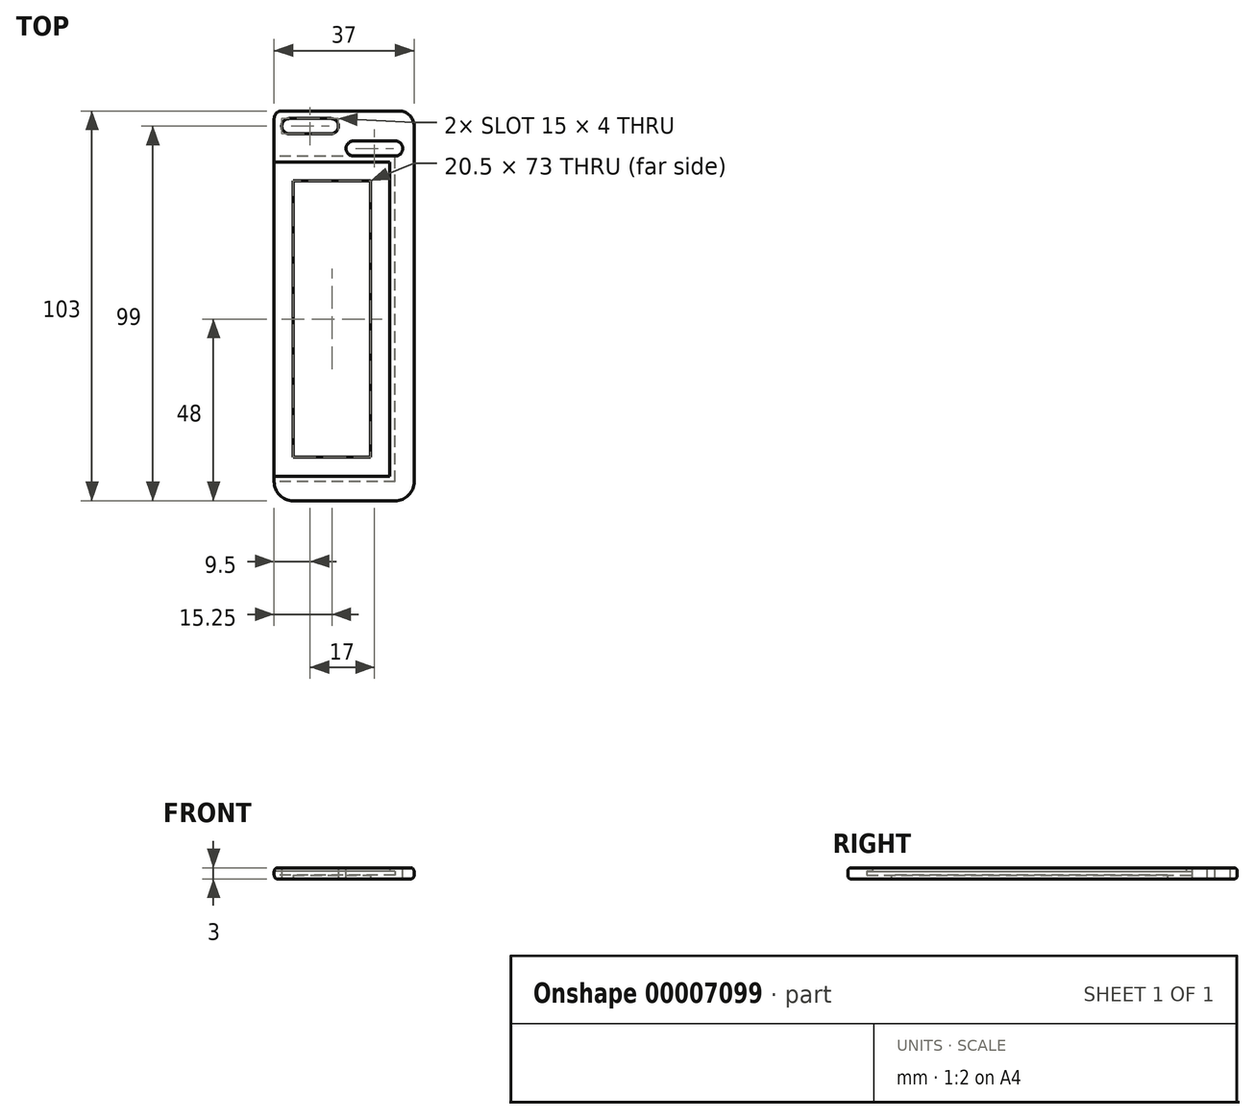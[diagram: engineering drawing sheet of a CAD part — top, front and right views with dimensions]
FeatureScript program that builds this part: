
annotation { "Feature Type Name" : "Feature", "Feature Type Description" : "" }
export const myFeature = defineFeature(function(context is Context, id is Id, definition is map)
    precondition{}
    {
        {
            var Q0;
            Q0=qCreatedBy(makeId("Top.planeOp"),FACE);
            var sketch = newSketch(context, id + "F0", { "sketchPlane" : qUnion([Q0])});
            skLineSegment(sketch, "E0.bottom", {"start": v(0, 0) * mm, "end": v(54, 0) * mm, "construction": true});
            skLineSegment(sketch, "E0.top", {"start": v(0, 86) * mm, "end": v(54, 86) * mm, "construction": true});
            skLineSegment(sketch, "E0.left", {"start": v(0, 0) * mm, "end": v(0, 86) * mm, "construction": true});
            skLineSegment(sketch, "E0.right", {"start": v(54, 0) * mm, "end": v(54, 86) * mm});
            skLineSegment(sketch, "E1", {"start": v(54, 0) * mm, "end": v(22, 0) * mm});
            skLineSegment(sketch, "E2", {"start": v(0, 43) * mm, "end": v(90.24, 43) * mm, "construction": true});
            skLineSegment(sketch, "E3.0.MirrorCS", {"start": v(54, 86) * mm, "end": v(22, 86) * mm});
            skLineSegment(sketch, "E4.0", {"start": v(59, 91) * mm, "end": v(22, 91) * mm});
            skLineSegment(sketch, "E4.1", {"start": v(59, -5) * mm, "end": v(59, 91) * mm});
            skLineSegment(sketch, "E4.2", {"start": v(59, -5) * mm, "end": v(22, -5) * mm});
            skLineSegment(sketch, "E5", {"start": v(22, 91) * mm, "end": v(22, 86) * mm});
            skLineSegment(sketch, "E6", {"start": v(22, -5) * mm, "end": v(22, 0) * mm});
            skSolve(sketch);
        }
        {
            var Q0;
            Q0 = qSketchRegion(id + "F0", true);
            extrude(context, id + "F1", {"entities" : qUnion([Q0]), "depth" : 1 * mm});
        }
        {
            var Q0;
            Q0=makeQuery(id+"F1.opExtrude","CAP_FACE",FACE,{"disambiguationData":[OSD([sQuery(id+"F0.wireOp",EDGE,"E0.right"),sQuery(id+"F0.wireOp",EDGE,"E1"),sQuery(id+"F0.wireOp",EDGE,"E3.0.MirrorCS"),sQuery(id+"F0.wireOp",EDGE,"E4.0"),sQuery(id+"F0.wireOp",EDGE,"E4.1"),sQuery(id+"F0.wireOp",EDGE,"E4.2"),sQuery(id+"F0.wireOp",EDGE,"E5"),sQuery(id+"F0.wireOp",EDGE,"E6")])],"isStart":false});
            var sketch = newSketch(context, id + "F2", { "sketchPlane" : qUnion([Q0])});
            skLineSegment(sketch, "E7.0", {"start": v(54, 86) * mm, "end": v(22, 86) * mm, "construction": true});
            skLineSegment(sketch, "E7.1", {"start": v(54, 0) * mm, "end": v(54, 86) * mm, "construction": true});
            skLineSegment(sketch, "E7.2", {"start": v(54, 0) * mm, "end": v(22, 0) * mm, "construction": true});
            skLineSegment(sketch, "E8.0", {"start": v(52.5, 84.5) * mm, "end": v(22, 84.5) * mm});
            skLineSegment(sketch, "E8.1", {"start": v(52.5, 1.5) * mm, "end": v(52.5, 84.5) * mm});
            skLineSegment(sketch, "E8.2", {"start": v(52.5, 1.5) * mm, "end": v(22, 1.5) * mm});
            skLineSegment(sketch, "E9.0", {"start": v(59, 91) * mm, "end": v(22, 91) * mm});
            skLineSegment(sketch, "E9.1", {"start": v(59, -5) * mm, "end": v(59, 91) * mm});
            skLineSegment(sketch, "E9.2", {"start": v(59, -5) * mm, "end": v(22, -5) * mm});
            skLineSegment(sketch, "E10", {"start": v(22, 84.5) * mm, "end": v(22, 91) * mm});
            skLineSegment(sketch, "E11", {"start": v(22, 1.5) * mm, "end": v(22, -5) * mm});
            skSolve(sketch);
        }
        {
            var Q0;
            Q0 = qSketchRegion(id + "F2", true);
            extrude(context, id + "F3", {"entities" : qUnion([Q0]), "operationType" : NewBodyOperationType.ADD, "depth" : 1 * mm});
        }
        {
            var Q0;
            Q0=makeQuery(id+"F1.opExtrude","CAP_FACE",FACE,{"disambiguationData":[OSD([sQuery(id+"F0.wireOp",EDGE,"E0.right"),sQuery(id+"F0.wireOp",EDGE,"E1"),sQuery(id+"F0.wireOp",EDGE,"E3.0.MirrorCS"),sQuery(id+"F0.wireOp",EDGE,"E4.0"),sQuery(id+"F0.wireOp",EDGE,"E4.1"),sQuery(id+"F0.wireOp",EDGE,"E4.2"),sQuery(id+"F0.wireOp",EDGE,"E5"),sQuery(id+"F0.wireOp",EDGE,"E6")])],"isStart":true});
            var sketch = newSketch(context, id + "F4", { "sketchPlane" : qUnion([Q0])});
            skLineSegment(sketch, "E12.0", {"start": v(59, 5) * mm, "end": v(59, -91) * mm});
            skLineSegment(sketch, "E12.1", {"start": v(59, 5) * mm, "end": v(22, 5) * mm});
            skLineSegment(sketch, "E12.2", {"start": v(59, -91) * mm, "end": v(22, -91) * mm});
            skLineSegment(sketch, "E12.3", {"start": v(22, -91) * mm, "end": v(22, -86) * mm});
            skLineSegment(sketch, "E12.4", {"start": v(22, -84.5) * mm, "end": v(22, -86) * mm});
            skLineSegment(sketch, "E12.5", {"start": v(52.5, -84.5) * mm, "end": v(22, -84.5) * mm});
            skLineSegment(sketch, "E12.6", {"start": v(52.5, -1.5) * mm, "end": v(52.5, -84.5) * mm});
            skLineSegment(sketch, "E12.7", {"start": v(52.5, -1.5) * mm, "end": v(22, -1.5) * mm});
            skLineSegment(sketch, "E12.8", {"start": v(22, 5) * mm, "end": v(22, 0) * mm});
            skLineSegment(sketch, "E12.9", {"start": v(22, -1.5) * mm, "end": v(22, 0) * mm});
            skSolve(sketch);
        }
        {
            var Q0;
            Q0 = qSketchRegion(id + "F4", true);
            extrude(context, id + "F5", {"entities" : qUnion([Q0]), "operationType" : NewBodyOperationType.ADD, "depth" : 1 * mm});
        }
        {
            var Q0;
            Q0=qCreatedBy(makeId("Top.planeOp"),FACE);
            var sketch = newSketch(context, id + "F6", { "sketchPlane" : qUnion([Q0])});
            skLineSegment(sketch, "E13.0", {"start": v(59, 91) * mm, "end": v(22, 91) * mm, "construction": true});
            skLineSegment(sketch, "E14.bottom", {"start": v(22, 91) * mm, "end": v(59, 91) * mm});
            skLineSegment(sketch, "E14.top", {"start": v(24, 98) * mm, "end": v(55, 98) * mm});
            skLineSegment(sketch, "E14.left", {"start": v(22, 91) * mm, "end": v(22, 96) * mm});
            skLineSegment(sketch, "E14.right", {"start": v(59, 91) * mm, "end": v(59, 94) * mm});
            skLineSegment(sketch, "E15", {"start": v(27, 75.52) * mm, "end": v(27, 108.91) * mm, "construction": true});
            skLineSegment(sketch, "E16.bottom", {"start": v(26, 96) * mm, "end": v(37, 96) * mm});
            skLineSegment(sketch, "E16.top", {"start": v(26, 92) * mm, "end": v(37, 92) * mm});
            skLineSegment(sketch, "E16.left", {"start": v(24, 94) * mm, "end": v(24, 94) * mm});
            skLineSegment(sketch, "E16.right", {"start": v(39, 94) * mm, "end": v(39, 94) * mm});
            skPoint(sketch, "E17.visualSharp", {"position": v(59, 98) * mm});
            skArc(sketch, "E17.filletArc", {"start": v(59, 94) * mm, "mid": v(57.83, 96.83) * mm, "end": v(55, 98) * mm});
            skPoint(sketch, "E18.visualSharp", {"position": v(22, 98) * mm});
            skArc(sketch, "E18.filletArc", {"start": v(24, 98) * mm, "mid": v(22.59, 97.41) * mm, "end": v(22, 96) * mm});
            skPoint(sketch, "E19.visualSharp", {"position": v(39, 96) * mm});
            skArc(sketch, "E19.filletArc", {"start": v(39, 94) * mm, "mid": v(38.41, 95.41) * mm, "end": v(37, 96) * mm});
            skPoint(sketch, "E20.visualSharp", {"position": v(39, 92) * mm});
            skArc(sketch, "E20.filletArc", {"start": v(37, 92) * mm, "mid": v(38.41, 92.59) * mm, "end": v(39, 94) * mm});
            skArc(sketch, "E21.filletArc", {"start": v(26, 96) * mm, "mid": v(24.59, 95.41) * mm, "end": v(24, 94) * mm});
            skPoint(sketch, "E22.visualSharp", {"position": v(24, 92) * mm});
            skArc(sketch, "E22.filletArc", {"start": v(24, 94) * mm, "mid": v(24.59, 92.59) * mm, "end": v(26, 92) * mm});
            skSolve(sketch);
        }
        {
            var Q0;
            Q0 = qSketchRegion(id + "F6", true);
            var Q1;
            Q1=makeQuery(id+"F3.opExtrude","CAP_FACE",FACE,{"disambiguationData":[OSD([sQuery(id+"F2.wireOp",EDGE,"E8.0"),sQuery(id+"F2.wireOp",EDGE,"E8.1"),sQuery(id+"F2.wireOp",EDGE,"E8.2"),sQuery(id+"F2.wireOp",EDGE,"E9.0"),sQuery(id+"F2.wireOp",EDGE,"E9.1"),sQuery(id+"F2.wireOp",EDGE,"E9.2"),sQuery(id+"F2.wireOp",EDGE,"E10"),sQuery(id+"F2.wireOp",EDGE,"E11")])],"isStart":false});
            extrude(context, id + "F7", {"entities" : qUnion([Q0]), "operationType" : NewBodyOperationType.ADD, "endBound" : BoundingType.UP_TO_SURFACE, "endBoundEntityFace" : qUnion([Q1]), "depth" : 25 * mm});
        }
        {
            var Q0;
            Q0 = qSketchRegion(id + "F6", true);
            var Q1;
            Q1=makeQuery(id+"F5.opExtrude","CAP_FACE",FACE,{"disambiguationData":[OSD([sQuery(id+"F4.wireOp",EDGE,"E12.0"),sQuery(id+"F4.wireOp",EDGE,"E12.1"),sQuery(id+"F4.wireOp",EDGE,"E12.2"),sQuery(id+"F4.wireOp",EDGE,"E12.3"),sQuery(id+"F4.wireOp",EDGE,"E12.4"),sQuery(id+"F4.wireOp",EDGE,"E12.5"),sQuery(id+"F4.wireOp",EDGE,"E12.6"),sQuery(id+"F4.wireOp",EDGE,"E12.7"),sQuery(id+"F4.wireOp",EDGE,"E12.8"),sQuery(id+"F4.wireOp",EDGE,"E12.9")])],"isStart":false});
            extrude(context, id + "F8", {"entities" : qUnion([Q0]), "operationType" : NewBodyOperationType.ADD, "endBound" : BoundingType.UP_TO_SURFACE, "oppositeDirection" : true, "endBoundEntityFace" : qUnion([Q1]), "depth" : 25 * mm});
        }
        {
            var Q0;
            Q0=makeQuery(id+"F5.boolean.opBoolean","MERGE",EDGE,{"derivedFrom":[makeQuery(id+"F3.boolean.opBoolean","MERGE",EDGE,{"derivedFrom":[makeQuery(id+"F1.opExtrude","SWEPT_EDGE",EDGE,{"disambiguationData":[OSD([sQuery(id+"F0.wireOp",EDGE,"E4.1"),sQuery(id+"F0.wireOp",EDGE,"E4.2")])]}),makeQuery(id+"F3.opExtrude","SWEPT_EDGE",EDGE,{"disambiguationData":[OSD([sQuery(id+"F2.wireOp",EDGE,"E9.1"),sQuery(id+"F2.wireOp",EDGE,"E9.2")])]})]}),makeQuery(id+"F5.opExtrude","SWEPT_EDGE",EDGE,{"disambiguationData":[OSD([sQuery(id+"F4.wireOp",EDGE,"E12.0"),sQuery(id+"F4.wireOp",EDGE,"E12.1")])]})]});
            var Q1;
            Q1=makeQuery(id+"F5.boolean.opBoolean","MERGE",EDGE,{"derivedFrom":[makeQuery(id+"F3.boolean.opBoolean","MERGE",EDGE,{"derivedFrom":[makeQuery(id+"F1.opExtrude","SWEPT_EDGE",EDGE,{"disambiguationData":[OSD([sQuery(id+"F0.wireOp",EDGE,"E4.2"),sQuery(id+"F0.wireOp",EDGE,"E6")])]}),makeQuery(id+"F3.opExtrude","SWEPT_EDGE",EDGE,{"disambiguationData":[OSD([sQuery(id+"F2.wireOp",EDGE,"E9.2"),sQuery(id+"F2.wireOp",EDGE,"E11")])]})]}),makeQuery(id+"F5.opExtrude","SWEPT_EDGE",EDGE,{"disambiguationData":[OSD([sQuery(id+"F4.wireOp",EDGE,"E12.1"),sQuery(id+"F4.wireOp",EDGE,"E12.8")])]})]});
            fillet(context, id + "F9", {"entities" : qUnion([Q0, Q1]), "radius" : 5 * mm, "tangentPropagation" : true, "allowEdgeOverflow" : false});
        }
        {
            var Q0;
            Q0=makeQuery(id+"F8.boolean.opBoolean","MERGE",FACE,{"derivedFrom":[makeQuery(id+"F5.opExtrude","CAP_FACE",FACE,{"disambiguationData":[OSD([sQuery(id+"F4.wireOp",EDGE,"E12.0"),sQuery(id+"F4.wireOp",EDGE,"E12.1"),sQuery(id+"F4.wireOp",EDGE,"E12.2"),sQuery(id+"F4.wireOp",EDGE,"E12.3"),sQuery(id+"F4.wireOp",EDGE,"E12.4"),sQuery(id+"F4.wireOp",EDGE,"E12.5"),sQuery(id+"F4.wireOp",EDGE,"E12.6"),sQuery(id+"F4.wireOp",EDGE,"E12.7"),sQuery(id+"F4.wireOp",EDGE,"E12.8"),sQuery(id+"F4.wireOp",EDGE,"E12.9")])],"isStart":false}),makeQuery(id+"F8.opExtrude","CAP_FACE",FACE,{"disambiguationData":[OSD([sQuery(id+"F6.wireOp",EDGE,"E14.bottom"),sQuery(id+"F6.wireOp",EDGE,"E14.top"),sQuery(id+"F6.wireOp",EDGE,"E14.left"),sQuery(id+"F6.wireOp",EDGE,"E14.right"),sQuery(id+"F6.wireOp",EDGE,"E16.bottom"),sQuery(id+"F6.wireOp",EDGE,"E16.top"),sQuery(id+"F6.wireOp",EDGE,"E17.filletArc"),sQuery(id+"F6.wireOp",EDGE,"E18.filletArc"),sQuery(id+"F6.wireOp",EDGE,"E19.filletArc"),sQuery(id+"F6.wireOp",EDGE,"E20.filletArc"),sQuery(id+"F6.wireOp",EDGE,"E21.filletArc"),sQuery(id+"F6.wireOp",EDGE,"E22.filletArc")])],"isStart":false})]});
            var sketch = newSketch(context, id + "F10", { "sketchPlane" : qUnion([Q0])});
            skLineSegment(sketch, "E23.1", {"start": v(52.5, -84.5) * mm, "end": v(22, -84.5) * mm});
            skLineSegment(sketch, "E23.2", {"start": v(52.5, -1.5) * mm, "end": v(52.5, -84.5) * mm});
            skLineSegment(sketch, "E23.3", {"start": v(52.5, -1.5) * mm, "end": v(22, -1.5) * mm});
            skLineSegment(sketch, "E24.0", {"start": v(47.5, -79.5) * mm, "end": v(27, -79.5) * mm});
            skLineSegment(sketch, "E24.1", {"start": v(47.5, -6.5) * mm, "end": v(47.5, -79.5) * mm});
            skLineSegment(sketch, "E24.2", {"start": v(47.5, -6.5) * mm, "end": v(27, -6.5) * mm});
            skLineSegment(sketch, "E25", {"start": v(22, -84.5) * mm, "end": v(22, -1.5) * mm});
            skLineSegment(sketch, "E26", {"start": v(27, -79.5) * mm, "end": v(27, -6.5) * mm});
            skSolve(sketch);
        }
        {
            var Q0;
            Q0 = qSketchRegion(id + "F10", true);
            var Q1;
            Q1=makeQuery(id+"F5.opExtrude","CAP_FACE",FACE,{"disambiguationData":[OSD([sQuery(id+"F4.wireOp",EDGE,"E12.0"),sQuery(id+"F4.wireOp",EDGE,"E12.1"),sQuery(id+"F4.wireOp",EDGE,"E12.2"),sQuery(id+"F4.wireOp",EDGE,"E12.3"),sQuery(id+"F4.wireOp",EDGE,"E12.4"),sQuery(id+"F4.wireOp",EDGE,"E12.5"),sQuery(id+"F4.wireOp",EDGE,"E12.6"),sQuery(id+"F4.wireOp",EDGE,"E12.7"),sQuery(id+"F4.wireOp",EDGE,"E12.8"),sQuery(id+"F4.wireOp",EDGE,"E12.9")])],"isStart":true});
            extrude(context, id + "F11", {"entities" : qUnion([Q0]), "operationType" : NewBodyOperationType.ADD, "endBound" : BoundingType.UP_TO_SURFACE, "oppositeDirection" : true, "endBoundEntityFace" : qUnion([Q1]), "depth" : 25 * mm});
        }
        {
            var Q0;
            Q0=makeQuery(id+"F11.boolean.opBoolean","MERGE",EDGE,{"derivedFrom":[makeQuery(id+"F8.boolean.opBoolean","MERGE",EDGE,{"derivedFrom":[makeQuery(id+"F5.opExtrude","CAP_EDGE",EDGE,{"disambiguationData":[OSD([sQuery(id+"F4.wireOp",EDGE,"E12.3"),sQuery(id+"F4.wireOp",EDGE,"E12.4")])],"isStart":false}),makeQuery(id+"F8.opExtrude","CAP_EDGE",EDGE,{"disambiguationData":[OSD([sQuery(id+"F6.wireOp",EDGE,"E14.left")])],"isStart":false})]}),makeQuery(id+"F5.opExtrude","CAP_EDGE",EDGE,{"disambiguationData":[OSD([sQuery(id+"F4.wireOp",EDGE,"E12.8"),sQuery(id+"F4.wireOp",EDGE,"E12.9")])],"isStart":false}),makeQuery(id+"F11.opExtrude","CAP_EDGE",EDGE,{"disambiguationData":[OSD([sQuery(id+"F10.wireOp",EDGE,"E25")])],"isStart":true})]});
            fillet(context, id + "F12", {"entities" : qUnion([Q0]), "radius" : 1 * mm, "tangentPropagation" : true, "allowEdgeOverflow" : false});
        }
        {
            var Q0;
            Q0=makeQuery(id+"F7.boolean.opBoolean","MERGE",EDGE,{"derivedFrom":[makeQuery(id+"F3.opExtrude","CAP_EDGE",EDGE,{"disambiguationData":[OSD([sQuery(id+"F2.wireOp",EDGE,"E10")])],"isStart":false}),makeQuery(id+"F7.opExtrude","CAP_EDGE",EDGE,{"disambiguationData":[OSD([sQuery(id+"F6.wireOp",EDGE,"E14.left")])],"isStart":false})]});
            fillet(context, id + "F13", {"entities" : qUnion([Q0]), "radius" : 1 * mm, "tangentPropagation" : true, "allowEdgeOverflow" : false});
        }
        {
            var Q0;
            Q0=makeQuery(id+"F7.boolean.opBoolean","MERGE",FACE,{"derivedFrom":[makeQuery(id+"F3.opExtrude","CAP_FACE",FACE,{"disambiguationData":[OSD([sQuery(id+"F2.wireOp",EDGE,"E8.0"),sQuery(id+"F2.wireOp",EDGE,"E8.1"),sQuery(id+"F2.wireOp",EDGE,"E8.2"),sQuery(id+"F2.wireOp",EDGE,"E9.0"),sQuery(id+"F2.wireOp",EDGE,"E9.1"),sQuery(id+"F2.wireOp",EDGE,"E9.2"),sQuery(id+"F2.wireOp",EDGE,"E10"),sQuery(id+"F2.wireOp",EDGE,"E11")])],"isStart":false}),makeQuery(id+"F7.opExtrude","CAP_FACE",FACE,{"disambiguationData":[OSD([sQuery(id+"F6.wireOp",EDGE,"E14.bottom"),sQuery(id+"F6.wireOp",EDGE,"E14.top"),sQuery(id+"F6.wireOp",EDGE,"E14.left"),sQuery(id+"F6.wireOp",EDGE,"E14.right"),sQuery(id+"F6.wireOp",EDGE,"E16.bottom"),sQuery(id+"F6.wireOp",EDGE,"E16.top"),sQuery(id+"F6.wireOp",EDGE,"E17.filletArc"),sQuery(id+"F6.wireOp",EDGE,"E18.filletArc"),sQuery(id+"F6.wireOp",EDGE,"E19.filletArc"),sQuery(id+"F6.wireOp",EDGE,"E20.filletArc"),sQuery(id+"F6.wireOp",EDGE,"E21.filletArc"),sQuery(id+"F6.wireOp",EDGE,"E22.filletArc")])],"isStart":false})]});
            var sketch = newSketch(context, id + "F14", { "sketchPlane" : qUnion([Q0])});
            skLineSegment(sketch, "E27.bottom", {"start": v(43, 86.1) * mm, "end": v(54, 86.1) * mm});
            skLineSegment(sketch, "E27.top", {"start": v(43, 90.1) * mm, "end": v(54, 90.1) * mm});
            skLineSegment(sketch, "E27.left", {"start": v(41, 88.1) * mm, "end": v(41, 88.1) * mm});
            skLineSegment(sketch, "E27.right", {"start": v(56, 88.1) * mm, "end": v(56, 88.1) * mm});
            skPoint(sketch, "E28.visualSharp", {"position": v(41, 90.1) * mm});
            skArc(sketch, "E28.filletArc", {"start": v(43, 90.1) * mm, "mid": v(41.59, 89.51) * mm, "end": v(41, 88.1) * mm});
            skPoint(sketch, "E29.visualSharp", {"position": v(56, 90.1) * mm});
            skArc(sketch, "E29.filletArc", {"start": v(56, 88.1) * mm, "mid": v(55.41, 89.51) * mm, "end": v(54, 90.1) * mm});
            skPoint(sketch, "E30.visualSharp", {"position": v(56, 86.1) * mm});
            skArc(sketch, "E30.filletArc", {"start": v(54, 86.1) * mm, "mid": v(55.41, 86.69) * mm, "end": v(56, 88.1) * mm});
            skPoint(sketch, "E31.visualSharp", {"position": v(41, 86.1) * mm});
            skArc(sketch, "E31.filletArc", {"start": v(41, 88.1) * mm, "mid": v(41.59, 86.69) * mm, "end": v(43, 86.1) * mm});
            skSolve(sketch);
        }
        {
            var Q0;
            Q0 = qSketchRegion(id + "F14", true);
            extrude(context, id + "F15", {"entities" : qUnion([Q0]), "operationType" : NewBodyOperationType.REMOVE, "endBound" : BoundingType.THROUGH_ALL, "oppositeDirection" : true, "depth" : 25 * mm});
        }
    });
